# Revit family: Plymold-Essentials-Quest_Seating-
name_source: partatom
category: Furniture
units: mm (PartAtom-declared; Revit-internal decimal feet)

## family parameters
Always vertical = Yes
Cut with Voids When Loaded = No
OmniClass Number = 23.40.20.00
OmniClass Title = General Furniture and Specialties
Render Appearance Source = Family Geometry
Room Calculation Point = No
Shared = No
Work Plane-Based = No

## types (6) — shared parameters
Assembly Code = E2020200
BACK MATERIAL = PLY - Solid Oak
Brand = Quest Rowback & Solidback
CAP MATERIAL = PLY - Plastic Black
Default Elevation = 0"
Depth = 18"
FRAME MATERIAL = PLY - Onyx Black Powdercoat
GLIDES MATERIAL = PLY - Plastic Black
Keynote = 12500
Manufacturer = Plymold
Product Documentation Link = https://plymold.com
Revit Model Built By = https://www.servex-us.com
Sustainability = https://plymold.com
Type Comments = Chairs & Barstools
URL = https://plymold.com
zero-valued in all types: Cost

## per-type parameters (varying)
| type | Chair | Description | Height | SEAT MATERIAL | Solid Seat | Solid-Wood Seat | Width |
| 6761PSF | Yes | Quest Solidback Metal Chair and Upholstered Seat - 16"W x 18"D x 31 1/4"H | 31 1/4" | PLY - Vinyl - Lite Gray | No | No | 16" |
| 6761SSF | Yes | Quest Solidback Metal Chair and Solid Oak Seat - 16"W x 18"D x 31 1/4"H | 31 1/4" | PLY - Solid Oak | No | Yes | 16" |
| 6761CSF | Yes | Quest Solidback Metal Chair and Composite Seat - 16"W x 18"D x 31 1/4"H | 31 1/4" | PLY - Plastic Atlantis | Yes | Yes | 16" |
| 6763CSF | No | Quest Solidback Metal Chair and Composite Seat - 16 1/4"W x 18"D x 43 1/4"H | 43 1/4" | PLY - Plastic Atlantis | Yes | Yes | 16 1/4" |
| 6763PSF | No | Quest Solidback Metal Chair and Upholstered Seat - 16 1/4"W x 18"D x 43 1/4"H | 43 1/4" | PLY - Vinyl - Lite Gray | No | No | 16 1/4" |
| 6763SSF | No | Quest Solidback Metal Chair and Solid Oak Seat - 16 1/4"W x 18"D x 43 1/4"H | 43 1/4" | PLY - Solid Oak | No | Yes | 16 1/4" |

note: column(s) folded — value = type name in every type: Model

## geometry (parser evidence)
native form markers: Sweep x4
no freeform markers — native parametric forms only
